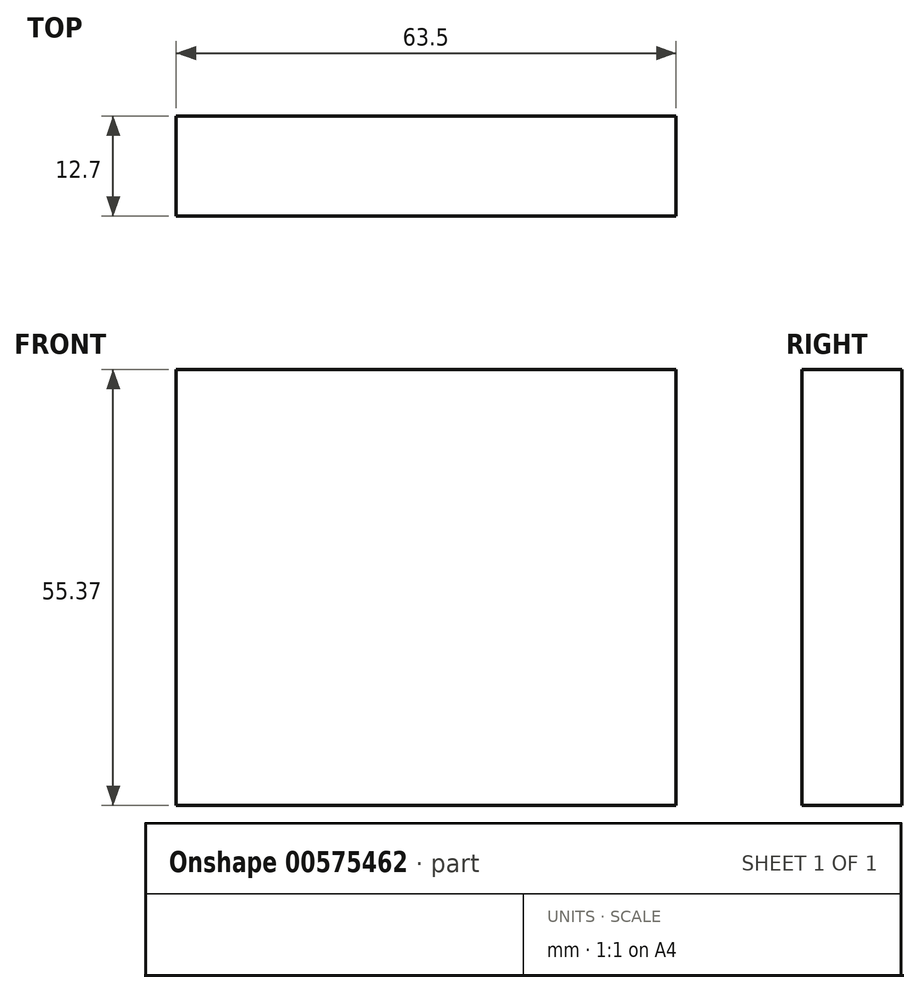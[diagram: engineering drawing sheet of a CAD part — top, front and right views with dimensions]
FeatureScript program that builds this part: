
annotation { "Feature Type Name" : "Feature", "Feature Type Description" : "" }
export const myFeature = defineFeature(function(context is Context, id is Id, definition is map)
    precondition{}
    {
        {
            var Q0;
            Q0=qCreatedBy(makeId("Front.planeOp"),FACE);
            var sketch = newSketch(context, id + "F0", { "sketchPlane" : qUnion([Q0])});
            skLineSegment(sketch, "E0.bottom", {"start": v(-32.2, 8.7) * mm, "end": v(31.3, 8.7) * mm});
            skLineSegment(sketch, "E0.top", {"start": v(-32.2, -46.67) * mm, "end": v(31.3, -46.67) * mm});
            skLineSegment(sketch, "E0.left", {"start": v(-32.2, 8.7) * mm, "end": v(-32.2, -46.67) * mm});
            skLineSegment(sketch, "E0.right", {"start": v(31.3, 8.7) * mm, "end": v(31.3, -46.67) * mm});
            skSolve(sketch);
        }
        {
            var Q0;
            Q0 = qSketchRegion(id + "F0", true);
            extrude(context, id + "F1", {"entities" : qUnion([Q0]), "depth" : 12.7 * mm, "offsetDistance" : 25.4 * mm});
        }
    });
